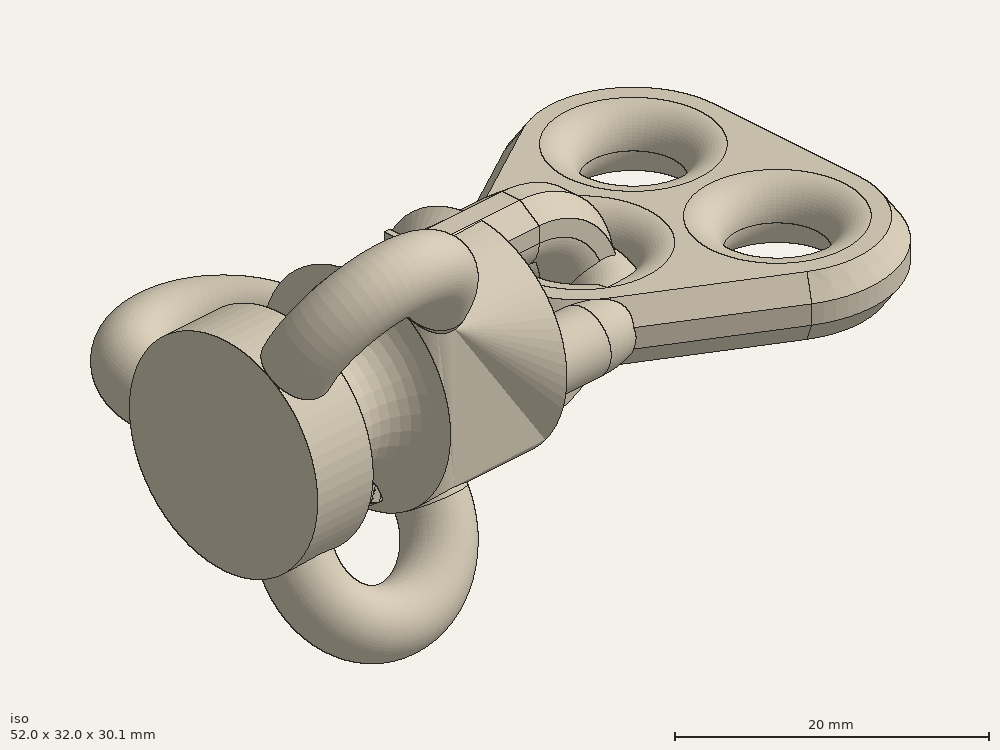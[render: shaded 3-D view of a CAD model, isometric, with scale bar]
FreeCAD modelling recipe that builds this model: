
FCSTD DOCUMENT  (FreeCAD 0.21R33771 (Git))
Label: _ChainLink
License: CreativeCommons Attribution
LicenseURL: http://creativecommons.org/licenses/by/4.0/
objects: Sketcher::SketchObject×22, PartDesign::Body×6, PartDesign::AdditivePipe×5, PartDesign::Pocket×4, PartDesign::Pad×3, App::DocumentObjectGroup×2, PartDesign::SubtractiveHelix×2, PartDesign::FeatureBase×1, PartDesign::SubtractivePipe×1, PartDesign::Fillet×1, PartDesign::Chamfer×1, PartDesign::Revolution×1, PartDesign::PolarPattern×1, Part::Feature×1, Mesh::Feature×1
note: 67 computed .brp shape members not serialized (recipe doc carries the construction recipe); baked Part::Feature solids carry a one-line shape summary decoded from their .brp

FEATURE [Sketcher::SketchObject] Sketch
  FullyConstrained = true
  MapMode = 5
  Placement = pos=(0,0,0) rot=(1,0,0;1.5708rad)
  Support = -> [XZ_Plane]
  sketch-geometry (5):
    g0: ArcOfCircle CenterX=-6.5 CenterY=0 CenterZ=0 NormalX=0 NormalY=0 NormalZ=1 AngleXU=0 Radius=6 StartAngle=1.5708 EndAngle=4.71239
    g1: LineSegment StartX=-6.5 StartY=-6 StartZ=0 EndX=6.50003 EndY=-6 EndZ=0
    g2: LineSegment StartX=-6.5 StartY=6 StartZ=0 EndX=6.50003 EndY=6 EndZ=0
    g3: ArcOfCircle CenterX=6.5 CenterY=0 CenterZ=0 NormalX=0 NormalY=0 NormalZ=1 AngleXU=0 Radius=6 StartAngle=0 EndAngle=1.57079
    g4: ArcOfCircle CenterX=6.5 CenterY=0 CenterZ=0 NormalX=0 NormalY=0 NormalZ=1 AngleXU=0 Radius=6 StartAngle=4.71239 EndAngle=6.28319
  constraints (14):
    c: Tangent(g0,g2) = 1.5708
    c: Tangent(g0,g1) = -1.5708
    c: Horizontal(g1)
    c: DistanceY(g0,g0) = 12
    c: PointOnObject(g0,g-1)
    c: Coincident(g3,g2)
    c: PointOnObject(g3,g-1)
    c: Coincident(g4,g3)
    c: Coincident(g4,g3)
    c: Coincident(g4,g1)
    c: Tangent(g2,g3)
    c: Tangent(g4,g1)
    c: Symmetric(g0,g3,g-2)
    c: DistanceX(g0,g3) = 13
FEATURE [Sketcher::SketchObject] Sketch001
  ExternalGeometry = -> [Sketch]
  FullyConstrained = true
  MapMode = 5
  Support = -> [XY_Plane]
  sketch-geometry (7):
    g0: Circle CenterX=12.5 CenterY=0 CenterZ=0 NormalX=0 NormalY=0 NormalZ=1 AngleXU=0 Radius=2.5
    g1: ArcOfCircle CenterX=12.5 CenterY=0 CenterZ=0 NormalX=0 NormalY=0 NormalZ=1 AngleXU=0 Radius=2.5 StartAngle=1.5708 EndAngle=4.71238
    g2: LineSegment StartX=12.5 StartY=2.5 StartZ=0 EndX=13.8014 EndY=2.5 EndZ=0
    g3: LineSegment StartX=13.8014 StartY=2.5 StartZ=0 EndX=15 EndY=0.788247 EndZ=0
    g4: LineSegment StartX=15 StartY=0.788247 StartZ=0 EndX=15 EndY=-0.788247 EndZ=0
    g5: LineSegment StartX=15 StartY=-0.788247 StartZ=0 EndX=13.8014 EndY=-2.5 EndZ=0
    g6: LineSegment StartX=13.8014 StartY=-2.5 StartZ=0 EndX=12.5 EndY=-2.5 EndZ=0
  constraints (17):
    c: Coincident(g0,g-3)
    c: Diameter(g0) = 5
    c: Coincident(g1,g0)
    c: Tangent(g1,g2) = 1.5708
    c: Coincident(g2,g3)
    c: Coincident(g3,g4)
    c: Coincident(g4,g5)
    c: Coincident(g5,g6)
    c: Coincident(g6,g1)
    c: Horizontal(g2)
    c: Horizontal(g6)
    c: Symmetric(g5,g2,g-1)
    c: Symmetric(g4,g3,g-1)
    c: Angle(g3,g5) = 1.91986
    c: Equal(g0,g1)
    c: Tangent(g3,g0)
    c: Tangent(g4,g0)
FEATURE [PartDesign::AdditivePipe] AdditivePipe
  AllowMultiFace = false
  AuxilleryCurvelinear = true
  AuxillerySpineTangent = false
  Binormal = (0,0,0)
  Mode = 0
  Profile = -> Sketch001
  Spine = -> Sketch
  SpineTangent = false
  Transformation = 0
  Transition = 0
FEATURE [PartDesign::Body] Body  label="Link"
  Group = -> [Sketch,Sketch001,AdditivePipe]
  Origin = -> Origin
  Tip = -> AdditivePipe
FEATURE [Sketcher::SketchObject] Sketch002
  FullyConstrained = false
  MapMode = 5
  Placement = pos=(0,0,0) rot=(1,0,0;1.5708rad)
  Support = -> [XZ_Plane001]
  sketch-geometry (4):
    g0: LineSegment StartX=0 StartY=-6 StartZ=0 EndX=6.50002 EndY=-6 EndZ=0
    g1: LineSegment StartX=-2.46425e-05 StartY=6 StartZ=0 EndX=6.5 EndY=6 EndZ=0
    g2: ArcOfCircle CenterX=6.5 CenterY=0 CenterZ=0 NormalX=0 NormalY=0 NormalZ=1 AngleXU=0 Radius=6 StartAngle=0 EndAngle=1.5708
    g3: ArcOfCircle CenterX=6.5 CenterY=0 CenterZ=0 NormalX=0 NormalY=0 NormalZ=1 AngleXU=0 Radius=6 StartAngle=4.71239 EndAngle=6.28319
  constraints (14):
    c: Horizontal(g0)
    c: Coincident(g2,g1)
    c: PointOnObject(g2,g-1)
    c: Coincident(g3,g2)
    c: Coincident(g3,g2)
    c: Coincident(g3,g0)
    c: Tangent(g1,g2)
    c: Tangent(g3,g0)
    c: DistanceY(g0,g1) = 12  'width'
    c: Horizontal(g1)
    c: PointOnObject(g2,g-1)
    c: DistanceX(g-1,g2) = 6.5
    c: Equal(g0,g1)
    c: PointOnObject(g0,g-2)
FEATURE [Sketcher::SketchObject] Sketch003
  ExternalGeometry = -> [Sketch002]
  FullyConstrained = false
  MapMode = 5
  Placement = pos=(0,0,0) rot=(0.57735,0.57735,0.57735;2.0944rad)
  Support = -> [YZ_Plane001]
  sketch-geometry (7):
    g0: ArcOfCircle CenterX=5e-16 CenterY=-6 CenterZ=0 NormalX=0 NormalY=0 NormalZ=1 AngleXU=0 Radius=2.5 StartAngle=3.14159 EndAngle=6.28319
    g1: ArcOfCircle CenterX=5e-16 CenterY=-6 CenterZ=0 NormalX=0 NormalY=0 NormalZ=1 AngleXU=0 Radius=2.5 StartAngle=-3.75438e-10 EndAngle=3.14159
    g2: LineSegment StartX=-2.5 StartY=-6 StartZ=0 EndX=-2.5 EndY=-7.30142 EndZ=0
    g3: LineSegment StartX=-2.5 StartY=-7.30142 StartZ=0 EndX=-0.788247 EndY=-8.5 EndZ=0
    g4: LineSegment StartX=-0.788247 StartY=-8.5 StartZ=0 EndX=0.788247 EndY=-8.5 EndZ=0
    g5: LineSegment StartX=0.788247 StartY=-8.5 StartZ=0 EndX=2.5 EndY=-7.30142 EndZ=0
    g6: LineSegment StartX=2.5 StartY=-7.30142 StartZ=0 EndX=2.5 EndY=-6 EndZ=0
  constraints (17):
    c: Coincident(g0,g-3)
    c: Coincident(g1,g0)
    c: Coincident(g1,g0)
    c: Coincident(g1,g0)
    c: Tangent(g1,g2) = -1.5708
    c: Coincident(g2,g3)
    c: Coincident(g3,g4)
    c: Coincident(g4,g5)
    c: Coincident(g5,g6)
    c: Vertical(g6)
    c: Coincident(g1,g6)
    c: Symmetric(g5,g2,g-2)
    c: Symmetric(g4,g3,g-2)
    c: Tangent(g4,g0)
    c: Angle(g5,g3) = 1.91986
    c: Diameter(g1) = 5
    c: Tangent(g5,g0)
FEATURE [Sketcher::SketchObject] Sketch004
  FullyConstrained = false
  MapMode = 5
  Placement = pos=(0,0,0) rot=(1,0,0;1.5708rad)
  Support = -> [XZ_Plane001]
  expr: Constraints[5] = Sketch002.Constraints.width
  sketch-geometry (30):
    g0: LineSegment StartX=-1.79014 StartY=6.96036 StartZ=0 EndX=1.84014 EndY=7.13964 EndZ=0
    g1: LineSegment StartX=2.05 StartY=6.93988 StartZ=0 EndX=2.05 EndY=5.06012 EndZ=0
    g2: LineSegment StartX=1.84014 StartY=4.86036 StartZ=0 EndX=-1.79014 EndY=5.03964 EndZ=0
    g3: LineSegment StartX=-2 StartY=6 StartZ=0 EndX=2 EndY=6 EndZ=0
    g4: LineSegment StartX=-2 StartY=-6 StartZ=0 EndX=2 EndY=-6 EndZ=0
    g5: LineSegment StartX=-2 StartY=6.95 StartZ=0 EndX=-2 EndY=5.05 EndZ=0
    g6: ArcOfCircle CenterX=1.85 CenterY=6.93988 CenterZ=0 NormalX=0 NormalY=0 NormalZ=1 AngleXU=0 Radius=0.2 StartAngle=-1.8e-15 EndAngle=1.62014
    g7: ArcOfCircle CenterX=1.85 CenterY=5.06012 CenterZ=0 NormalX=0 NormalY=0 NormalZ=1 AngleXU=0 Radius=0.2 StartAngle=4.66305 EndAngle=6.28319
    g8: LineSegment StartX=2.05 StartY=7.15 StartZ=0 EndX=2.05 EndY=4.85 EndZ=0
    g9: LineSegment StartX=1.79001 StartY=-5.2395 StartZ=0 EndX=-1.79001 EndY=-5.0605 EndZ=0
    g10: LineSegment StartX=-2 StartY=-5.05 StartZ=0 EndX=-2 EndY=-6.95 EndZ=0
    g11: LineSegment StartX=2 StartY=-6.96025 StartZ=0 EndX=2 EndY=-9 EndZ=0
    g12: LineSegment StartX=2 StartY=-9 StartZ=0 EndX=-3 EndY=-9 EndZ=0
    g13: LineSegment StartX=-3 StartY=-9 StartZ=0 EndX=-3 EndY=-3 EndZ=0
    g14: LineSegment StartX=-3 StartY=-3 StartZ=0 EndX=2 EndY=-3 EndZ=0
    g15: LineSegment StartX=2 StartY=-3 StartZ=0 EndX=2 EndY=-5.03975 EndZ=0
    g16: LineSegment StartX=-2 StartY=7.16012 StartZ=0 EndX=-2 EndY=9 EndZ=0
    g17: LineSegment StartX=-2 StartY=9 StartZ=0 EndX=-2.5 EndY=9 EndZ=0
    g18: LineSegment StartX=-2.5 StartY=9 StartZ=0 EndX=-2.5 EndY=3 EndZ=0
    g19: LineSegment StartX=-2.5 StartY=3 StartZ=0 EndX=-2 EndY=3 EndZ=0
    g20: LineSegment StartX=-2 StartY=3 StartZ=0 EndX=-2 EndY=4.83988 EndZ=0
    g21: ArcOfCircle CenterX=-1.8 CenterY=7.16012 CenterZ=0 NormalX=0 NormalY=0 NormalZ=1 AngleXU=0 Radius=0.2 StartAngle=3.14159 EndAngle=4.76173
    g22: ArcOfCircle CenterX=-1.8 CenterY=4.83988 CenterZ=0 NormalX=0 NormalY=0 NormalZ=1 AngleXU=0 Radius=0.2 StartAngle=1.52145 EndAngle=3.14159
    g23: LineSegment StartX=-2 StartY=-5.26025 StartZ=0 EndX=-2 EndY=-6.73975 EndZ=0
    g24: ArcOfCircle CenterX=-1.8 CenterY=-5.26025 CenterZ=0 NormalX=0 NormalY=0 NormalZ=1 AngleXU=0 Radius=0.2 StartAngle=1.52084 EndAngle=3.14159
    g25: ArcOfCircle CenterX=-1.8 CenterY=-6.73975 CenterZ=0 NormalX=0 NormalY=0 NormalZ=1 AngleXU=0 Radius=0.2 StartAngle=3.14159 EndAngle=4.76235
    g26: LineSegment StartX=-1.79001 StartY=-6.9395 StartZ=0 EndX=1.79001 EndY=-6.7605 EndZ=0
    g27: ArcOfCircle CenterX=1.8 CenterY=-5.03975 CenterZ=0 NormalX=0 NormalY=0 NormalZ=1 AngleXU=0 Radius=0.2 StartAngle=4.66243 EndAngle=6.28319
    g28: ArcOfCircle CenterX=1.8 CenterY=-6.96025 CenterZ=0 NormalX=0 NormalY=0 NormalZ=1 AngleXU=0 Radius=0.2 StartAngle=0 EndAngle=1.62075
    g29: LineSegment StartX=2 StartY=-5.25 StartZ=0 EndX=2 EndY=-6.75 EndZ=0
  constraints (80):
    c: Vertical(g1)
    c: Horizontal(g4)
    c: DistanceX(g4,g-1) = 2
    c: DistanceX(g4,g4) = 4
    c: Symmetric(g4,g3,g-1)
    c: DistanceY(g4,g3) = 12
    c: Equal(g4,g3)
    c: PointOnObject(g3,g5)
    c: DistanceY(g5,g5) = 1.9
    c: Tangent(g0,g6) = 1.5708
    c: Tangent(g1,g6) = 1.5708
    c: Tangent(g2,g7) = 1.5708
    c: Tangent(g1,g7) = 1.5708
    c: Vertical(g8)
    c: Tangent(g8,g6)
    c: Symmetric(g8,g8,g3)
    c: Symmetric(g6,g7,g3)
    c: DistanceX(g3,g8) = 0.05
    c: PointOnObject(g8,g2)
    c: DistanceY(g8,g8) = 2.3
    c: Radius(g7) = 0.2
    c: Vertical(g11)
    c: Coincident(g11,g12)
    c: Horizontal(g12)
    c: Coincident(g12,g13)
    c: Coincident(g13,g14)
    c: Horizontal(g14)
    c: Coincident(g14,g15)
    c: Vertical(g15)
    c: PointOnObject(g4,g10)
    c: DistanceY(g10,g10) = 1.9
    c: Symmetric(g12,g13,g4)
    c: DistanceY(g13,g13) = 6
    c: DistanceX(g13,g-1) = 3
    c: PointOnObject(g4,g11)
    c: Vertical(g16)
    c: Coincident(g16,g17)
    c: Horizontal(g17)
    c: Coincident(g17,g18)
    c: Coincident(g18,g19)
    c: Horizontal(g19)
    c: Coincident(g19,g20)
    c: Vertical(g20)
    c: Symmetric(g17,g18,g3)
    c: Tangent(g0,g21) = -1.5708
    c: Tangent(g16,g21) = 1.5708
    c: Tangent(g2,g22) = -1.5708
    c: Tangent(g20,g22) = 1.5708
    c: Symmetric(g5,g5,g3)
    c: PointOnObject(g5,g0)
    c: PointOnObject(g5,g2)
    c: Radius(g21) = 0.2
    c: Symmetric(g21,g22,g3)
    c: PointOnObject(g20,g5)
    c: DistanceX(g17,g17) = 0.5
    c: DistanceY(g18,g18) = 6
    c: PointOnObject(g23,g10)
    c: Vertical(g23)
    c: Coincident(g24,g23)
    c: Coincident(g25,g23)
    c: Symmetric(g10,g10,g4)
    c: Coincident(g24,g9)
    c: Tangent(g9,g24)
    c: Tangent(g24,g23)
    c: Tangent(g23,g25)
    c: Symmetric(g25,g24,g4)
    c: Radius(g25) = 0.2
    c: Tangent(g26,g25) = -1.5708
    c: PointOnObject(g10,g9)
    c: Tangent(g9,g27) = 1.5708
    c: Tangent(g15,g27) = 1.5708
    c: Tangent(g26,g28) = 1.5708
    c: Tangent(g11,g28) = 1.5708
    c: Symmetric(g28,g27,g4)
    c: PointOnObject(g4,g29)
    c: Symmetric(g29,g29,g4)
    c: DistanceY(g29,g29) = 1.5
    c: PointOnObject(g29,g9)
    c: PointOnObject(g29,g26)
    c: Radius(g28) = 0.2
FEATURE [PartDesign::AdditivePipe] AdditivePipe001
  AllowMultiFace = false
  AuxilleryCurvelinear = true
  AuxillerySpineTangent = false
  Binormal = (0,0,0)
  Mode = 0
  Placement = pos=(0,0,0) rot=(0.57735,0.57735,0.57735;2.0944rad)
  Profile = -> Sketch003
  Spine = -> Sketch002
  SpineTangent = false
  Transformation = 0
  Transition = 0
FEATURE [Sketcher::SketchObject] Sketch005
  FullyConstrained = false
  MapMode = 5
  Placement = pos=(0,0,0) rot=(0.57735,0.57735,0.57735;2.0944rad)
  Support = -> [YZ_Plane001]
  sketch-geometry (10):
    g0: LineSegment StartX=-2.5 StartY=8.5 StartZ=0 EndX=2.5 EndY=8.5 EndZ=0
    g1: LineSegment StartX=2.5 StartY=8.5 StartZ=0 EndX=2.5 EndY=3.5 EndZ=0
    g2: LineSegment StartX=2.5 StartY=3.5 StartZ=0 EndX=-2.5 EndY=3.5 EndZ=0
    g3: LineSegment StartX=-2.5 StartY=3.5 StartZ=0 EndX=-2.5 EndY=8.5 EndZ=0
    g4: LineSegment StartX=-2.5 StartY=-3.5 StartZ=0 EndX=2.5 EndY=-3.5 EndZ=0
    g5: LineSegment StartX=2.5 StartY=-3.5 StartZ=0 EndX=2.5 EndY=-8.5 EndZ=0
    g6: LineSegment StartX=2.5 StartY=-8.5 StartZ=0 EndX=-2.5 EndY=-8.5 EndZ=0
    g7: LineSegment StartX=-2.5 StartY=-8.5 StartZ=0 EndX=-2.5 EndY=-3.5 EndZ=0
    g8: LineSegment StartX=2.5 StartY=6 StartZ=0 EndX=-2.5 EndY=6 EndZ=0
    g9: LineSegment StartX=2.5 StartY=-6 StartZ=0 EndX=-2.5 EndY=-6 EndZ=0
  constraints (28):
    c: Coincident(g0,g1)
    c: Coincident(g1,g2)
    c: Coincident(g2,g3)
    c: Coincident(g3,g0)
    c: Horizontal(g0)
    c: Vertical(g1)
    c: Vertical(g3)
    c: Coincident(g4,g5)
    c: Coincident(g5,g6)
    c: Coincident(g6,g7)
    c: Coincident(g7,g4)
    c: Horizontal(g6)
    c: Vertical(g5)
    c: Vertical(g7)
    c: Symmetric(g2,g4,g-1)
    c: Symmetric(g1,g4,g-1)
    c: Symmetric(g4,g4,g-2)
    c: Equal(g2,g3)
    c: Equal(g3,g4)
    c: Equal(g4,g7)
    c: PointOnObject(g8,g1)
    c: PointOnObject(g9,g5)
    c: PointOnObject(g9,g7)
    c: PointOnObject(g8,g3)
    c: Symmetric(g1,g0,g8)
    c: Symmetric(g5,g4,g9)
    c: DistanceY(g9,g8) = 12
    c: DistanceX(g0,g0) = 5
FEATURE [PartDesign::Pad] Pad
  AllowMultiFace = false
  BaseFeature = -> AdditivePipe001
  Direction = (1,1,1)
  Length = 5
  Length2 = 100
  Midplane = true
  Placement = pos=(0,0,0) rot=(0.57735,0.57735,0.57735;2.0944rad)
  Profile = -> Sketch005
  Type = 0
FEATURE [PartDesign::Pocket] Pocket
  AllowMultiFace = false
  BaseFeature = -> Pad
  Direction = (1,1,1)
  Length = 5
  Length2 = 100
  Midplane = true
  Placement = pos=(0,0,0) rot=(0.57735,0.57735,0.57735;2.0944rad)
  Profile = -> Sketch004
  Type = 1
FEATURE [PartDesign::Body] Body001  label="HalfLink1"
  Group = -> [Sketch002,Sketch003,Sketch004,AdditivePipe001,Sketch005,Pad,Pocket]
  Origin = -> Origin001
  Tip = -> Pocket
FEATURE [PartDesign::FeatureBase] Clone
  BaseFeature = -> Body001
FEATURE [PartDesign::Body] Body002  label="HalfLink2"
  BaseFeature = -> Body001
  Group = -> [Clone]
  Origin = -> Origin002
  Placement = pos=(0,0,0) rot=(0,1,0;3.14159rad)
  Tip = -> Clone
FEATURE [Sketcher::SketchObject] Sketch006
  FullyConstrained = false
  MapMode = 5
  Support = -> [XY_Plane003]
  sketch-geometry (13):
    g0: LineSegment StartX=0 StartY=6.5 StartZ=0 EndX=0 EndY=-6.5 EndZ=0
    g1: LineSegment StartX=0 StartY=-6.5 StartZ=0 EndX=-11.2583 EndY=-9e-16 EndZ=0
    g2: LineSegment StartX=-11.2583 StartY=-9e-16 StartZ=0 EndX=0 EndY=6.5 EndZ=0
    g3: LineSegment StartX=8.6 StartY=0 StartZ=0 EndX=8.6 EndY=6.5 EndZ=0
    g4: ArcOfCircle CenterX=0 CenterY=6.5 CenterZ=0 NormalX=0 NormalY=0 NormalZ=1 AngleXU=0 Radius=8.6 StartAngle=0 EndAngle=2.0944
    g5: LineSegment StartX=-4.3 StartY=13.9478 StartZ=0 EndX=-15.5583 EndY=7.44782 EndZ=0
    g6: ArcOfCircle CenterX=-11.2583 CenterY=-9e-16 CenterZ=0 NormalX=0 NormalY=0 NormalZ=1 AngleXU=0 Radius=8.6 StartAngle=2.0944 EndAngle=4.18879
    g7: LineSegment StartX=-15.5583 StartY=-7.44782 StartZ=0 EndX=-4.29996 EndY=-13.9478 EndZ=0
    g8: ArcOfCircle CenterX=0 CenterY=-6.5 CenterZ=0 NormalX=0 NormalY=0 NormalZ=1 AngleXU=0 Radius=8.6 StartAngle=4.18879 EndAngle=6.28319
    g9: LineSegment StartX=8.6 StartY=-6.5 StartZ=0 EndX=8.6 EndY=0 EndZ=0
    g10: Circle CenterX=-11.2583 CenterY=-9e-16 CenterZ=0 NormalX=0 NormalY=0 NormalZ=1 AngleXU=0 Radius=3.5
    g11: Circle CenterX=0 CenterY=6.5 CenterZ=0 NormalX=0 NormalY=0 NormalZ=1 AngleXU=0 Radius=3.5
    g12: Circle CenterX=0 CenterY=-6.5 CenterZ=0 NormalX=0 NormalY=0 NormalZ=1 AngleXU=0 Radius=3.5
  constraints (31):
    c: Coincident(g0,g1)
    c: Coincident(g1,g2)
    c: Coincident(g2,g0)
    c: Symmetric(g0,g0,g-1)
    c: Equal(g0,g1)
    c: Equal(g1,g2)
    c: DistanceY(g0,g0) = 13
    c: PointOnObject(g3,g-1)
    c: Vertical(g3)
    c: Tangent(g3,g4) = -1.5708
    c: Tangent(g4,g5) = -1.5708
    c: Tangent(g5,g6) = -1.5708
    c: Tangent(g6,g7) = -1.5708
    c: Coincident(g6,g1)
    c: Coincident(g0,g4)
    c: Coincident(g8,g0)
    c: Coincident(g8,g7)
    c: Coincident(g9,g8)
    c: Coincident(g9,g3)
    c: Vertical(g9)
    c: Equal(g4,g8)
    c: Equal(g8,g6)
    c: Tangent(g8,g7)
    c: PointOnObject(g-1,g0)
    c: Radius(g4) = 8.6
    c: Coincident(g10,g6)
    c: Coincident(g11,g4)
    c: Coincident(g12,g8)
    c: Equal(g10,g11)
    c: Equal(g11,g12)
    c: Radius(g10) = 3.5
FEATURE [PartDesign::Pad] Pad001
  AllowMultiFace = false
  Direction = (1,1,1)
  Length = 5
  Length2 = 100
  Midplane = true
  Profile = -> Sketch006
  Type = 0
FEATURE [Sketcher::SketchObject] Sketch007
  FullyConstrained = false
  MapMode = 5
  Support = -> [XY_Plane003]
  sketch-geometry (10):
    g0: LineSegment StartX=0 StartY=6.5 StartZ=0 EndX=0 EndY=-6.5 EndZ=0
    g1: LineSegment StartX=0 StartY=-6.5 StartZ=0 EndX=-11.2583 EndY=0 EndZ=0
    g2: LineSegment StartX=-11.2583 StartY=0 StartZ=0 EndX=0 EndY=6.5 EndZ=0
    g3: LineSegment StartX=8.75 StartY=0 StartZ=0 EndX=8.75 EndY=6.5 EndZ=0
    g4: ArcOfCircle CenterX=0 CenterY=6.5 CenterZ=0 NormalX=0 NormalY=0 NormalZ=1 AngleXU=0 Radius=8.75 StartAngle=0 EndAngle=2.0944
    g5: LineSegment StartX=-4.375 StartY=14.0777 StartZ=0 EndX=-15.6333 EndY=7.57772 EndZ=0
    g6: ArcOfCircle CenterX=-11.2583 CenterY=0 CenterZ=0 NormalX=0 NormalY=0 NormalZ=1 AngleXU=0 Radius=8.75 StartAngle=2.0944 EndAngle=4.18879
    g7: LineSegment StartX=-15.6333 StartY=-7.57772 StartZ=0 EndX=-4.375 EndY=-14.0777 EndZ=0
    g8: ArcOfCircle CenterX=0 CenterY=-6.5 CenterZ=0 NormalX=0 NormalY=0 NormalZ=1 AngleXU=0 Radius=8.75 StartAngle=4.18879 EndAngle=6.28319
    g9: LineSegment StartX=8.75 StartY=-6.5 StartZ=0 EndX=8.75 EndY=0 EndZ=0
  constraints (25):
    c: Coincident(g0,g1)
    c: Coincident(g1,g2)
    c: Coincident(g2,g0)
    c: Symmetric(g0,g0,g-1)
    c: Equal(g0,g1)
    c: Equal(g1,g2)
    c: DistanceY(g0,g0) = 13
    c: PointOnObject(g3,g-1)
    c: Vertical(g3)
    c: Tangent(g3,g4) = -1.5708
    c: Tangent(g4,g5) = -1.5708
    c: Tangent(g5,g6) = -1.5708
    c: Tangent(g6,g7) = -1.5708
    c: Coincident(g6,g1)
    c: Coincident(g0,g4)
    c: Coincident(g8,g0)
    c: Coincident(g8,g7)
    c: Coincident(g9,g8)
    c: Coincident(g9,g3)
    c: Vertical(g9)
    c: Equal(g4,g8)
    c: Equal(g8,g6)
    c: Tangent(g8,g7)
    c: PointOnObject(g-1,g0)
    c: Radius(g4) = 8.75
FEATURE [Sketcher::SketchObject] Sketch008
  FullyConstrained = false
  MapMode = 5
  Placement = pos=(0,0,0) rot=(1,0,0;1.5708rad)
  Support = -> [XZ_Plane003]
  sketch-geometry (7):
    g0: LineSegment StartX=7.2314 StartY=2.6 StartZ=0 EndX=8.5 EndY=0.788247 EndZ=0
    g1: LineSegment StartX=8.5 StartY=0.788247 StartZ=0 EndX=8.5 EndY=-0.788247 EndZ=0
    g2: LineSegment StartX=8.5 StartY=-0.788247 StartZ=0 EndX=7.2314 EndY=-2.6 EndZ=0
    g3: LineSegment StartX=7.2314 StartY=-2.6 StartZ=0 EndX=9 EndY=-2.6 EndZ=0
    g4: LineSegment StartX=9 StartY=-2.6 StartZ=0 EndX=9 EndY=2.6 EndZ=0
    g5: LineSegment StartX=9 StartY=2.6 StartZ=0 EndX=7.2314 EndY=2.6 EndZ=0
    g6: Circle CenterX=6 CenterY=0 CenterZ=0 NormalX=0 NormalY=0 NormalZ=1 AngleXU=0 Radius=2.5
  constraints (19):
    c: Coincident(g0,g1)
    c: Coincident(g1,g2)
    c: Coincident(g2,g3)
    c: Horizontal(g3)
    c: Coincident(g3,g4)
    c: Coincident(g4,g5)
    c: Coincident(g5,g0)
    c: Horizontal(g5)
    c: Symmetric(g1,g0,g-1)
    c: Diameter(g6) = 5
    c: Tangent(g6,g1)
    c: Angle(g0,g2) = 1.91986
    c: Tangent(g0,g6)
    c: Tangent(g2,g6)
    c: DistanceX(g0,g4) = 0.5
    c: Symmetric(g4,g3,g-1)
    c: DistanceY(g4,g4) = 5.2
    c: PointOnObject(g6,g-1)
    c: DistanceX(g-1,g6) = 6
FEATURE [PartDesign::SubtractivePipe] SubtractivePipe
  AllowMultiFace = false
  AuxilleryCurvelinear = true
  AuxillerySpineTangent = false
  BaseFeature = -> Pad001
  Binormal = (0,0,0)
  Mode = 0
  Profile = -> Sketch008
  Spine = -> Sketch007
  SpineTangent = false
  Transformation = 0
  Transition = 0
FEATURE [PartDesign::Fillet] Fillet
  Base = -> SubtractivePipe [Edge8,Edge9,Edge10,Edge26,Edge28,Edge30]
  BaseFeature = -> SubtractivePipe
  Radius = 2.498
  SupportTransform = false
  UseAllEdges = false
FEATURE [PartDesign::Body] Body003  label="TripleLink"
  Group = -> [Sketch006,Pad001,Sketch007,Sketch008,SubtractivePipe,Fillet]
  Origin = -> Origin003
  Placement = pos=(24,0,0) rot=(0,0,1;0rad)
  Tip = -> Fillet
FEATURE [App::DocumentObjectGroup] Group  label="HalfLink"
  Group = -> [Body001,Body002]
FEATURE [Sketcher::SketchObject] Sketch009
  FullyConstrained = true
  MapMode = 5
  Placement = pos=(0,0,0) rot=(1,0,0;1.5708rad)
  Support = -> [XZ_Plane004]
  sketch-geometry (3):
    g0: ArcOfCircle CenterX=-6 CenterY=0 CenterZ=0 NormalX=0 NormalY=0 NormalZ=1 AngleXU=0 Radius=6 StartAngle=1.5708 EndAngle=4.71239
    g1: LineSegment StartX=-6 StartY=-6 StartZ=0 EndX=0 EndY=-6 EndZ=0
    g2: LineSegment StartX=-6 StartY=6 StartZ=0 EndX=0 EndY=6 EndZ=0
  constraints (9):
    c: Tangent(g0,g1) = -1.5708
    c: Horizontal(g1)
    c: PointOnObject(g0,g-1)
    c: PointOnObject(g1,g-2)
    c: DistanceX(g1,g1) = 6
    c: Radius(g0) = 6
    c: Horizontal(g2)
    c: Tangent(g2,g0) = 1.5708
    c: PointOnObject(g2,g-2)
FEATURE [Sketcher::SketchObject] Sketch010
  ExternalGeometry = -> [Sketch009]
  FullyConstrained = true
  MapMode = 5
  Placement = pos=(0,0,0) rot=(0.57735,0.57735,0.57735;2.0944rad)
  Support = -> [YZ_Plane004]
  sketch-geometry (1):
    g0: Circle CenterX=2.7e-15 CenterY=-6 CenterZ=0 NormalX=0 NormalY=0 NormalZ=1 AngleXU=0 Radius=2.5
  constraints (2):
    c: Diameter(g0) = 5
    c: Coincident(g-3,g0)
FEATURE [PartDesign::AdditivePipe] AdditivePipe002
  AuxilleryCurvelinear = true
  AuxillerySpineTangent = false
  Binormal = (0,0,0)
  Mode = 0
  Placement = pos=(0,0,0) rot=(0.57735,0.57735,0.57735;2.0944rad)
  Profile = -> Sketch010
  Spine = -> Sketch009
  SpineTangent = false
  Transformation = 0
  Transition = 0
FEATURE [Sketcher::SketchObject] Sketch011
  ExternalGeometry = -> [Sketch009]
  FullyConstrained = true
  MapMode = 5
  Placement = pos=(0,0,0) rot=(1,0,0;1.5708rad)
  Support = -> [XZ_Plane004]
  sketch-geometry (6):
    g0: LineSegment StartX=-5.39 StartY=-3.4745 StartZ=0 EndX=-5 EndY=-4.15 EndZ=0
    g1: LineSegment StartX=-5 StartY=-4.15 StartZ=0 EndX=-4.61 EndY=-3.4745 EndZ=0
    g2: LineSegment StartX=-4.61 StartY=-3.4745 StartZ=0 EndX=-5.39 EndY=-3.4745 EndZ=0
    g3: LineSegment StartX=-5.39 StartY=-3.4745 StartZ=0 EndX=-5.0866 EndY=-4 EndZ=0
    g4: ArcOfCircle CenterX=-5 CenterY=-3.95 CenterZ=0 NormalX=0 NormalY=0 NormalZ=1 AngleXU=0 Radius=0.1 StartAngle=3.66519 EndAngle=5.75959
    g5: LineSegment StartX=-4.9134 StartY=-4 StartZ=0 EndX=-4.61 EndY=-3.4745 EndZ=0
  constraints (16):
    c: Coincident(g0,g1)
    c: Coincident(g1,g2)
    c: Coincident(g2,g0)
    c: Horizontal(g2)
    c: Equal(g2,g0)
    c: Equal(g0,g1)
    c: Coincident(g2,g3)
    c: Tangent(g3,g4) = -1.5708
    c: Tangent(g4,g5) = -1.5708
    c: PointOnObject(g4,g1)
    c: PointOnObject(g3,g0)
    c: Coincident(g5,g2)
    c: Radius(g4) = 0.1
    c: DistanceX(g2,g2) = 0.78
    c: DistanceY(g-3,g0) = 1.85
    c: DistanceX(g0,g-1) = 5
FEATURE [PartDesign::Chamfer] Chamfer
  Angle = 45
  Base = -> AdditivePipe002 [Edge7,Edge1]
  BaseFeature = -> AdditivePipe002
  ChamferType = 0
  FlipDirection = false
  Placement = pos=(0,0,0) rot=(0.57735,0.57735,0.57735;2.0944rad)
  Size = 0.5
  Size2 = 1
  SupportTransform = false
  UseAllEdges = false
FEATURE [PartDesign::SubtractiveHelix] SubtractiveHelix
  Angle = 0
  Axis = (1,0,0)
  Base = (-6,1.3e-15,-6)
  BaseFeature = -> Chamfer
  Growth = 0
  HasBeenEdited = true
  Height = 5.2
  LeftHanded = false
  Mode = 0
  Outside = false
  Pitch = 0.8
  Placement = pos=(0,0,0) rot=(0.57735,0.57735,0.57735;2.0944rad)
  Profile = -> Sketch011
  ReferenceAxis = -> Sketch009 [Edge3]
  Turns = 6.5
FEATURE [Sketcher::SketchObject] Sketch012
  ExternalGeometry = -> [Sketch009]
  FullyConstrained = true
  MapMode = 5
  Placement = pos=(0,0,0) rot=(1,0,0;1.5708rad)
  Support = -> [XZ_Plane004]
  expr: Constraints[12] = Sketch011.Constraints[12]
  expr: Constraints[13] = Sketch011.Constraints[13]
  expr: Constraints[14] = Sketch011.Constraints[14]
  expr: Constraints[15] = Sketch011.Constraints[15]
  sketch-geometry (6):
    g0: LineSegment StartX=-5.39 StartY=-3.4745 StartZ=0 EndX=-5 EndY=-4.15 EndZ=0
    g1: LineSegment StartX=-5 StartY=-4.15 StartZ=0 EndX=-4.61 EndY=-3.4745 EndZ=0
    g2: LineSegment StartX=-4.61 StartY=-3.4745 StartZ=0 EndX=-5.39 EndY=-3.4745 EndZ=0
    g3: LineSegment StartX=-5.39 StartY=-3.4745 StartZ=0 EndX=-5.0866 EndY=-4 EndZ=0
    g4: ArcOfCircle CenterX=-5 CenterY=-3.95 CenterZ=0 NormalX=0 NormalY=0 NormalZ=1 AngleXU=0 Radius=0.1 StartAngle=3.66519 EndAngle=5.75959
    g5: LineSegment StartX=-4.9134 StartY=-4 StartZ=0 EndX=-4.61 EndY=-3.4745 EndZ=0
  constraints (16):
    c: Coincident(g0,g1)
    c: Coincident(g1,g2)
    c: Coincident(g2,g0)
    c: Horizontal(g2)
    c: Equal(g2,g0)
    c: Equal(g0,g1)
    c: Coincident(g2,g3)
    c: Tangent(g3,g4) = -1.5708
    c: Tangent(g4,g5) = -1.5708
    c: PointOnObject(g4,g1)
    c: PointOnObject(g3,g0)
    c: Coincident(g5,g2)
    c: Radius(g4) = 0.1
    c: DistanceX(g2,g2) = 0.78
    c: DistanceY(g-3,g0) = 1.85
    c: DistanceX(g0,g-1) = 5
FEATURE [PartDesign::Pocket] Pocket001
  BaseFeature = -> SubtractiveHelix
  Direction = (0,1,2e-16)
  Length = 5
  Length2 = 5
  Placement = pos=(0,0,0) rot=(0.57735,0.57735,0.57735;2.0944rad)
  Profile = -> Sketch012
  ReferenceAxis = -> Sketch012 [N_Axis]
  Type = 0
FEATURE [Sketcher::SketchObject] Sketch013
  ExternalGeometry = -> [Sketch009]
  FullyConstrained = true
  MapMode = 5
  Placement = pos=(0,0,0) rot=(1,0,0;1.5708rad)
  Support = -> [XZ_Plane004]
  expr: Constraints[14] = Sketch011.Constraints[13]
  expr: Constraints[15] = Sketch011.Constraints[14]
  expr: Constraints[7] = Sketch011.Constraints[12]
  sketch-geometry (6):
    g0: LineSegment StartX=-5.2 StartY=7.85 StartZ=0 EndX=-4.81 EndY=8.5255 EndZ=0
    g1: LineSegment StartX=-4.81 StartY=8.5255 StartZ=0 EndX=-5.59 EndY=8.5255 EndZ=0
    g2: LineSegment StartX=-5.59 StartY=8.5255 StartZ=0 EndX=-5.2 EndY=7.85 EndZ=0
    g3: LineSegment StartX=-4.81 StartY=8.5255 StartZ=0 EndX=-5.1134 EndY=8 EndZ=0
    g4: ArcOfCircle CenterX=-5.2 CenterY=8.05 CenterZ=0 NormalX=0 NormalY=0 NormalZ=1 AngleXU=0 Radius=0.1 StartAngle=3.66519 EndAngle=5.75959
    g5: LineSegment StartX=-5.2866 StartY=8 StartZ=0 EndX=-5.59 EndY=8.5255 EndZ=0
  constraints (16):
    c: Coincident(g0,g1)
    c: Coincident(g1,g2)
    c: Coincident(g2,g0)
    c: Coincident(g1,g3)
    c: Tangent(g3,g4) = 1.5708
    c: Tangent(g4,g5) = 1.5708
    c: Coincident(g5,g1)
    c: Radius(g4) = 0.1
    c: PointOnObject(g4,g2)
    c: PointOnObject(g3,g0)
    c: Equal(g2,g0)
    c: Equal(g0,g1)
    c: DistanceX(g0,g-3) = 5.2
    c: Horizontal(g1)
    c: DistanceX(g1,g1) = 0.78
    c: DistanceY(g-3,g0) = 1.85
FEATURE [PartDesign::SubtractiveHelix] SubtractiveHelix001
  Angle = 0
  Axis = (1,0,0)
  Base = (-6,-1.3e-15,6)
  BaseFeature = -> Pocket001
  Growth = 0
  HasBeenEdited = true
  Height = 5.3
  LeftHanded = false
  Mode = 0
  Outside = false
  Pitch = 0.8
  Placement = pos=(0,0,0) rot=(0.57735,0.57735,0.57735;2.0944rad)
  Profile = -> Sketch013
  ReferenceAxis = -> Sketch009 [Edge1]
  Turns = 6.625
FEATURE [Sketcher::SketchObject] Sketch014
  ExternalGeometry = -> [Sketch009]
  FullyConstrained = true
  MapMode = 5
  Placement = pos=(0,0,0) rot=(1,0,0;1.5708rad)
  Support = -> [XZ_Plane004]
  expr: Constraints[12] = Sketch013.Constraints[12]
  expr: Constraints[14] = Sketch013.Constraints[14]
  expr: Constraints[15] = Sketch013.Constraints[15]
  expr: Constraints[7] = Sketch013.Constraints[7]
  sketch-geometry (6):
    g0: LineSegment StartX=-5.2 StartY=7.85 StartZ=0 EndX=-4.81 EndY=8.5255 EndZ=0
    g1: LineSegment StartX=-4.81 StartY=8.5255 StartZ=0 EndX=-5.59 EndY=8.5255 EndZ=0
    g2: LineSegment StartX=-5.59 StartY=8.5255 StartZ=0 EndX=-5.2 EndY=7.85 EndZ=0
    g3: LineSegment StartX=-4.81 StartY=8.5255 StartZ=0 EndX=-5.1134 EndY=8 EndZ=0
    g4: ArcOfCircle CenterX=-5.2 CenterY=8.05 CenterZ=0 NormalX=0 NormalY=0 NormalZ=1 AngleXU=0 Radius=0.1 StartAngle=3.66519 EndAngle=5.75959
    g5: LineSegment StartX=-5.2866 StartY=8 StartZ=0 EndX=-5.59 EndY=8.5255 EndZ=0
  constraints (16):
    c: Coincident(g0,g1)
    c: Coincident(g1,g2)
    c: Coincident(g2,g0)
    c: Coincident(g1,g3)
    c: Tangent(g3,g4) = 1.5708
    c: Tangent(g4,g5) = 1.5708
    c: Coincident(g5,g1)
    c: Radius(g4) = 0.1
    c: PointOnObject(g4,g2)
    c: PointOnObject(g3,g0)
    c: Equal(g2,g0)
    c: Equal(g0,g1)
    c: DistanceX(g0,g-3) = 5.2
    c: Horizontal(g1)
    c: DistanceX(g1,g1) = 0.78
    c: DistanceY(g-3,g0) = 1.85
FEATURE [PartDesign::Pocket] Pocket002
  BaseFeature = -> SubtractiveHelix001
  Direction = (0,1,2e-16)
  Length = 5
  Length2 = 5
  Placement = pos=(0,0,0) rot=(0.57735,0.57735,0.57735;2.0944rad)
  Profile = -> Sketch014
  ReferenceAxis = -> Sketch014 [N_Axis]
  Type = 0
FEATURE [PartDesign::Body] Body004  label="ConnLink1"
  Group = -> [Sketch009,Sketch010,AdditivePipe002,Sketch011,Chamfer,SubtractiveHelix,Sketch012,Pocket001,Sketch013,SubtractiveHelix001,Sketch014,Pocket002]
  Origin = -> Origin004
  Tip = -> Pocket002
FEATURE [App::DocumentObjectGroup] Group001  label="ConnLink"
  Group = -> [Body004]
FEATURE [Sketcher::SketchObject] Sketch015
  FullyConstrained = true
  MapMode = 5
  Support = -> [XY_Plane005]
  sketch-geometry (4):
    g0: ArcOfCircle CenterX=7 CenterY=0 CenterZ=0 NormalX=0 NormalY=0 NormalZ=1 AngleXU=0 Radius=6 StartAngle=4.71239 EndAngle=7.85398
    g1: LineSegment StartX=7 StartY=6 StartZ=0 EndX=0 EndY=6 EndZ=0
    g2: LineSegment StartX=7 StartY=-6 StartZ=0 EndX=0 EndY=-6 EndZ=0
    g3: Circle CenterX=7 CenterY=0 CenterZ=0 NormalX=0 NormalY=0 NormalZ=1 AngleXU=0 Radius=3.5
  constraints (11):
    c: PointOnObject(g0,g-1)
    c: DistanceX(g-1,g0) = 7
    c: PointOnObject(g1,g-2)
    c: Horizontal(g1)
    c: PointOnObject(g2,g-2)
    c: Horizontal(g2)
    c: Tangent(g2,g0) = 1.5708
    c: Tangent(g1,g0) = -1.5708
    c: DistanceY(g2,g1) = 12
    c: Coincident(g3,g0)
    c: Diameter(g3) = 7
FEATURE [Sketcher::SketchObject] Sketch016
  ExternalGeometry = -> [Sketch015]
  FullyConstrained = true
  MapMode = 5
  Placement = pos=(0,0,0) rot=(0.57735,0.57735,0.57735;2.0944rad)
  Support = -> [YZ_Plane005]
  sketch-geometry (1):
    g0: Circle CenterX=-6 CenterY=0 CenterZ=0 NormalX=0 NormalY=0 NormalZ=1 AngleXU=0 Radius=2.5
  constraints (2):
    c: Coincident(g0,g-3)
    c: Diameter(g0) = 5
FEATURE [PartDesign::AdditivePipe] AdditivePipe003
  AuxilleryCurvelinear = true
  AuxillerySpineTangent = false
  Binormal = (0,0,0)
  Mode = 0
  Placement = pos=(0,0,0) rot=(0.57735,0.57735,0.57735;2.0944rad)
  Profile = -> Sketch016
  Refine = true
  Spine = -> Sketch015
  SpineTangent = false
  Transformation = 0
  Transition = 0
FEATURE [Sketcher::SketchObject] Sketch018
  FullyConstrained = true
  MapMode = 5
  Support = -> [XY_Plane005]
  sketch-geometry (1):
    g0: Circle CenterX=-11 CenterY=8.5 CenterZ=0 NormalX=0 NormalY=0 NormalZ=1 AngleXU=0 Radius=6
  constraints (3):
    c: Diameter(g0) = 12
    c: DistanceX(g0,g-1) = 11
    c: DistanceY(g-1,g0) = 8.5
FEATURE [Sketcher::SketchObject] Sketch019
  AttachmentOffset = pos=(0,0,-8.5) rot=(0,0,1;0rad)
  ExternalGeometry = -> [Sketch018]
  FullyConstrained = true
  MapMode = 5
  Placement = pos=(0,8.5,1.9e-15) rot=(1,0,0;1.5708rad)
  Support = -> [XZ_Plane005]
  expr: .AttachmentOffset.Base.z = -Sketch018.Constraints[2]
  sketch-geometry (1):
    g0: Circle CenterX=-5 CenterY=0 CenterZ=0 NormalX=0 NormalY=0 NormalZ=1 AngleXU=0 Radius=2.5
  constraints (2):
    c: Coincident(g0,g-3)
    c: Diameter(g0) = 5
FEATURE [Sketcher::SketchObject] Sketch021
  FullyConstrained = true
  MapMode = 5
  Support = -> [XY_Plane005]
  sketch-geometry (6):
    g0: LineSegment StartX=-19.5 StartY=0 StartZ=0 EndX=-2.5 EndY=0 EndZ=0
    g1: LineSegment StartX=-2.5 StartY=0 StartZ=0 EndX=-2.5 EndY=8.5 EndZ=0
    g2: LineSegment StartX=-2.5 StartY=8.5 StartZ=0 EndX=-7.5 EndY=8.5 EndZ=0
    g3: ArcOfCircle CenterX=-11 CenterY=8.5 CenterZ=0 NormalX=0 NormalY=0 NormalZ=1 AngleXU=0 Radius=3.5 StartAngle=3.14159 EndAngle=6.28319
    g4: LineSegment StartX=-14.5 StartY=8.5 StartZ=0 EndX=-19.5 EndY=8.5 EndZ=0
    g5: LineSegment StartX=-19.5 StartY=8.5 StartZ=0 EndX=-19.5 EndY=0 EndZ=0
  constraints (19):
    c: Coincident(g0,g1)
    c: Coincident(g1,g2)
    c: Horizontal(g0)
    c: Horizontal(g2)
    c: Vertical(g1)
    c: Coincident(g2,g3)
    c: DistanceY(g1,g1) = 8.5
    c: DistanceX(g3,g-1) = 11
    c: Radius(g3) = 3.5
    c: DistanceX(g0,g-1) = 2.5
    c: PointOnObject(g0,g-1)
    c: Perpendicular(g3,g2)
    c: Horizontal(g2,g3)
    c: Coincident(g3,g4)
    c: Coincident(g4,g5)
    c: Coincident(g5,g0)
    c: Vertical(g5)
    c: DistanceX(g0,g0) = 17
    c: Horizontal(g4)
FEATURE [Sketcher::SketchObject] Sketch017
  FullyConstrained = true
  MapMode = 5
  Placement = pos=(0,0,0) rot=(0.57735,0.57735,0.57735;2.0944rad)
  Support = -> [YZ_Plane005]
  sketch-geometry (1):
    g0: Circle CenterX=0 CenterY=0 CenterZ=0 NormalX=0 NormalY=0 NormalZ=1 AngleXU=0 Radius=12
  constraints (2):
    c: Coincident(g0,g-1)
    c: Diameter(g0) = 24
FEATURE [PartDesign::Pad] Pad002
  BaseFeature = -> AdditivePipe003
  Direction = (1,-2e-16,3e-16)
  Length = 6
  Length2 = 10
  Midplane = true
  Placement = pos=(0,0,0) rot=(0.57735,0.57735,0.57735;2.0944rad)
  Profile = -> Sketch017
  ReferenceAxis = -> Sketch017 [N_Axis]
  Refine = true
  Type = 0
FEATURE [Sketcher::SketchObject] Sketch020
  FullyConstrained = true
  MapMode = 5
  Placement = pos=(0,0,0) rot=(0.57735,0.57735,0.57735;2.0944rad)
  Support = -> [YZ_Plane005]
  sketch-geometry (2):
    g0: Circle CenterX=0 CenterY=0 CenterZ=0 NormalX=0 NormalY=0 NormalZ=1 AngleXU=0 Radius=8.5
    g1: Circle CenterX=0 CenterY=0 CenterZ=0 NormalX=0 NormalY=0 NormalZ=1 AngleXU=0 Radius=15
  constraints (4):
    c: Coincident(g0,g-1)
    c: Coincident(g1,g0)
    c: Diameter(g1) = 30
    c: Diameter(g0) = 17
FEATURE [PartDesign::Pocket] Pocket003
  BaseFeature = -> Pad002
  Direction = (-1,2e-16,-3e-16)
  Length = 5
  Length2 = 5
  Midplane = true
  Placement = pos=(0,0,0) rot=(0.57735,0.57735,0.57735;2.0944rad)
  Profile = -> Sketch020
  ReferenceAxis = -> Sketch020 [N_Axis]
  Refine = true
  Type = 1
FEATURE [PartDesign::Revolution] Revolution
  Angle = 360
  Axis = (1,0,0)
  Base = (0,0,0)
  BaseFeature = -> Pocket003
  Placement = pos=(0,0,0) rot=(0.57735,0.57735,0.57735;2.0944rad)
  Profile = -> Sketch021
  ReferenceAxis = -> Sketch021 [H_Axis]
  Refine = true
FEATURE [PartDesign::AdditivePipe] AdditivePipe004
  AuxilleryCurvelinear = true
  AuxillerySpineTangent = false
  BaseFeature = -> Revolution
  Binormal = (0,0,0)
  Mode = 0
  Placement = pos=(0,0,0) rot=(0.57735,0.57735,0.57735;2.0944rad)
  Profile = -> Sketch019
  Refine = true
  Spine = -> Sketch018
  SpineTangent = false
  Transformation = 0
  Transition = 0
FEATURE [PartDesign::PolarPattern] PolarPattern
  Angle = 360
  Axis = -> X_Axis005
  BaseFeature = -> AdditivePipe004
  Occurrences = 3
  Originals = -> [AdditivePipe004]
  Placement = pos=(0,0,0) rot=(0.57735,0.57735,0.57735;2.0944rad)
  Refine = true
FEATURE [PartDesign::Body] Body005  label="QuadroLink"
  Group = -> [Sketch015,Sketch016,AdditivePipe003,Sketch017,Pad002,Sketch018,Sketch019,Sketch020,Pocket003,Sketch021,Revolution,AdditivePipe004,PolarPattern]
  Origin = -> Origin005
  Tip = -> PolarPattern
FEATURE [Part::Feature] Body006  label="QuadroLink001"
  shape: bbox 36.4 x 27.7 x 31.07 mm, 19 faces (baked)
FEATURE [Mesh::Feature] Mesh  label="QuadroLink001 (Meshed)"
